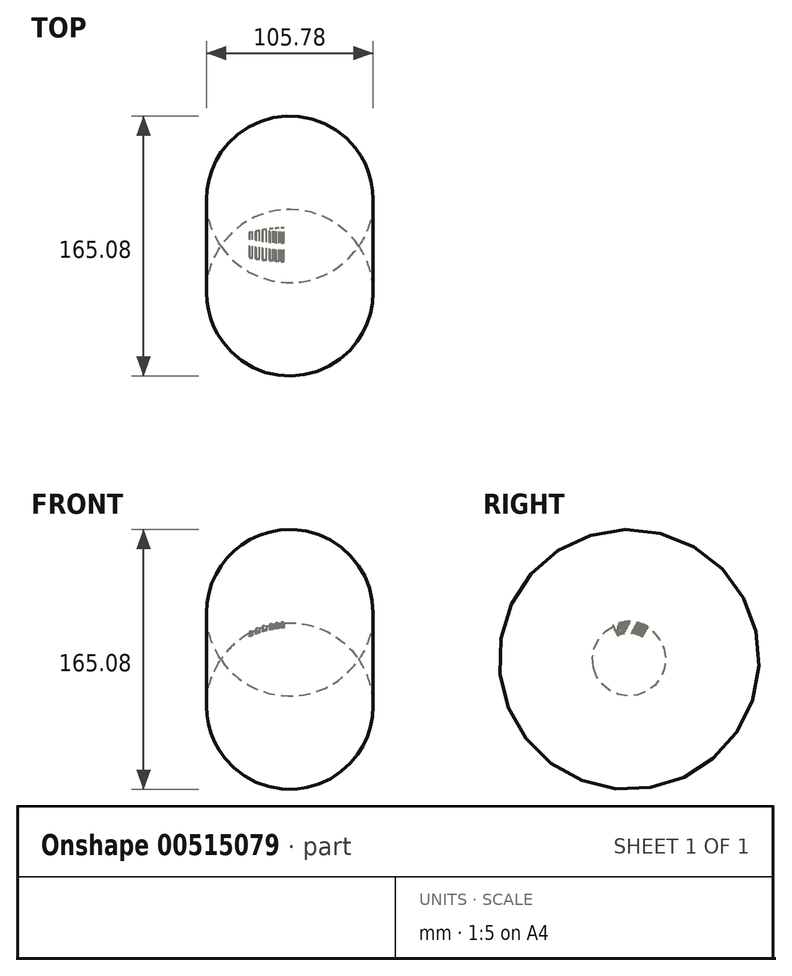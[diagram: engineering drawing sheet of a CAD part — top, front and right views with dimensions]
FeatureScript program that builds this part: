
annotation { "Feature Type Name" : "Feature", "Feature Type Description" : "" }
export const myFeature = defineFeature(function(context is Context, id is Id, definition is map)
    precondition{}
    {
        {
            var Q0;
            Q0=qCreatedBy(makeId("Front.planeOp"),FACE);
            var sketch = newSketch(context, id + "F0", { "sketchPlane" : qUnion([Q0])});
            skLineSegment(sketch, "E0", {"start": v(-43.8, 0) * mm, "end": v(43.8, 0) * mm});
            skArc(sketch, "E1", {"start": v(43.8, 0) * mm, "mid": v(0, 23.24) * mm, "end": v(-43.8, 0) * mm});
            skSolve(sketch);
        }
        {
            var Q0;
            Q0=makeQuery(id+"F0.imprint","IMPRINT",FACE,{"disambiguationData":[TD([[makeQuery(id+"F0.imprint","IMPRINT",EDGE,{"derivedFrom":sQuery(id+"F0.wireOp",EDGE,"E0")}),1.0]])]});
            var Q1;
            Q1=sQuery(id+"F0.wireOp",EDGE,"E0");
            revolve(context, id + "F1", {"entities" : qUnion([Q0]), "axis" : qUnion([Q1]), "revolveType" : RevolveType.FULL});
        }
        {
            var Q0;
            Q0=qCreatedBy(makeId("Front.planeOp"),FACE);
            var sketch = newSketch(context, id + "F2", { "sketchPlane" : qUnion([Q0])});
            skArc(sketch, "E2.0", {"start": v(43.8, 0) * mm, "mid": v(0, 23.24) * mm, "end": v(-43.8, 0) * mm});
            skLineSegment(sketch, "E3", {"start": v(-25.6, 16.62) * mm, "end": v(-25.13, 18.12) * mm});
            skLineSegment(sketch, "E4", {"start": v(-25.13, 18.12) * mm, "end": v(-23.65, 17.65) * mm});
            skLineSegment(sketch, "E5", {"start": v(-23.65, 17.65) * mm, "end": v(-21.86, 18.5) * mm});
            skLineSegment(sketch, "E6", {"start": v(-21.86, 18.5) * mm, "end": v(-21.12, 20.01) * mm});
            skLineSegment(sketch, "E7", {"start": v(-21.12, 20.01) * mm, "end": v(-19.33, 19.58) * mm});
            skLineSegment(sketch, "E8", {"start": v(-19.33, 19.58) * mm, "end": v(-17.47, 20.27) * mm});
            skLineSegment(sketch, "E9", {"start": v(-17.47, 20.27) * mm, "end": v(-17, 21.56) * mm});
            skLineSegment(sketch, "E10", {"start": v(-17, 21.56) * mm, "end": v(-14.88, 21.1) * mm});
            skLineSegment(sketch, "E11", {"start": v(-14.88, 21.1) * mm, "end": v(-12.92, 21.63) * mm});
            skLineSegment(sketch, "E12", {"start": v(-12.92, 21.63) * mm, "end": v(-12.37, 22.87) * mm});
            skLineSegment(sketch, "E13", {"start": v(-12.37, 22.87) * mm, "end": v(-10.72, 22.14) * mm});
            skLineSegment(sketch, "E14", {"start": v(-10.72, 22.14) * mm, "end": v(-9.29, 22.42) * mm});
            skLineSegment(sketch, "E15", {"start": v(-9.29, 22.42) * mm, "end": v(-8.53, 23.39) * mm});
            skLineSegment(sketch, "E16", {"start": v(-8.53, 23.39) * mm, "end": v(-6.8, 22.8) * mm});
            skLineSegment(sketch, "E17", {"start": v(-6.8, 22.8) * mm, "end": v(-5.66, 22.93) * mm});
            skLineSegment(sketch, "E18", {"start": v(-5.66, 22.93) * mm, "end": v(-4.64, 24.08) * mm});
            skLineSegment(sketch, "E19", {"start": v(-4.64, 24.08) * mm, "end": v(-3.57, 23.12) * mm});
            skSolve(sketch);
        }
        {
            var Q0;
            {var subQ0=sQuery(id+"F2.wireOp",EDGE,"E3");Q0=makeQuery(id+"F2.imprint","IMPRINT",FACE,{"disambiguationData":[TD([[makeQuery(id+"F2.imprint","IMPRINT",EDGE,{"derivedFrom":subQ0}),-1.0]])]});}
            var Q1;
            {var subQ0=sQuery(id+"F2.wireOp",EDGE,"E6");Q1=makeQuery(id+"F2.imprint","IMPRINT",FACE,{"disambiguationData":[TD([[makeQuery(id+"F2.imprint","IMPRINT",EDGE,{"derivedFrom":subQ0}),-1.0]])]});}
            var Q2;
            {var subQ0=sQuery(id+"F2.wireOp",EDGE,"E9");Q2=makeQuery(id+"F2.imprint","IMPRINT",FACE,{"disambiguationData":[TD([[makeQuery(id+"F2.imprint","IMPRINT",EDGE,{"derivedFrom":subQ0}),-1.0]])]});}
            var Q3;
            {var subQ0=sQuery(id+"F2.wireOp",EDGE,"E12");Q3=makeQuery(id+"F2.imprint","IMPRINT",FACE,{"disambiguationData":[TD([[makeQuery(id+"F2.imprint","IMPRINT",EDGE,{"derivedFrom":subQ0}),-1.0]])]});}
            var Q4;
            {var subQ0=sQuery(id+"F2.wireOp",EDGE,"E15");Q4=makeQuery(id+"F2.imprint","IMPRINT",FACE,{"disambiguationData":[TD([[makeQuery(id+"F2.imprint","IMPRINT",EDGE,{"derivedFrom":subQ0}),-1.0]])]});}
            var Q5;
            {var subQ0=sQuery(id+"F2.wireOp",EDGE,"E18");Q5=makeQuery(id+"F2.imprint","IMPRINT",FACE,{"disambiguationData":[TD([[makeQuery(id+"F2.imprint","IMPRINT",EDGE,{"derivedFrom":subQ0}),-1.0]])]});}
            var Q6;
            Q6=sQuery(id+"F0.wireOp",EDGE,"E0");
            revolve(context, id + "F3", {"operationType" : NewBodyOperationType.ADD, "entities" : qUnion([Q0, Q1, Q2, Q3, Q4, Q5]), "axis" : qUnion([Q6]), "revolveType" : RevolveType.TWO_DIRECTIONS, "angle" : 25 * degree, "angleBack" : 330 * degree});
        }
    });
